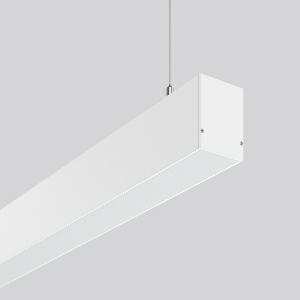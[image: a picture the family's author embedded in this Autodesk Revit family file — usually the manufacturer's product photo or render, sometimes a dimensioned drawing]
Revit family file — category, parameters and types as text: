
# Revit family: less_is_more_50_312313_002_5587
name_source: partatom
category: Lighting Fixtures
units: mm (PartAtom-declared; Revit-internal decimal feet)

## family parameters
Cut with Voids When Loaded = No
Host = Face
Light Source = No
Part Type = Normal
Room Calculation Point = No
Round Connector Dimension = Use Diameter
Shared = No

## types (1)
- LESS IS MORE 50 (1 x LED Modul 830, 3850 lm, 3000)
    Apparent Load = 34 VA
    CIE Flux Codes = 48 79 95 100 100
    Color Rendering = 80
    Color Temperature = 3000
    Default Elevation = 1800 mm
    Description = Series: LESS IS MORE 50
Linear pendant luminaire for aesthetically sophisticated lighting. Housing: extruded aluminium profile, powder-coated. End cap aluminium powder-coated. Canopy made of aluminium, powder-coated. Diffuser made of non-yellowing plastic (PMMA), opal. Direct light emission. Suitable for pendant. 2-point steel cable suspension freely positionable and infinitely height-adjustable. Special lengths available on request. LED unit with integrated converter interchangeable and removable. Suitable for through-wiring. With sensors or as a safety luminaire on request. 
Colour: traffic white, matt (RAL 9016)
Length: 1407 mm
Width: 57 mm
Height: 75 mm
Suspension length: 2000 mm
Lamp: LED
Socket: without socket
Colour temperature: 3000K
Colour rendering index (CRI): 80
System power: 34 W
Rated luminous flux: 3850 lm
Luminous efficiency: 113 lm/W
Control gear: Regulated power supply
Protection class: I
Type of protection: IP 20
    Height = 75 mm
    Lamp = 1 x LED Modul 830
    Lamp Light Flux = 3850 lm
    Lamp count = 1
    Length = 1407 mm
    Lifetime = 50000 h
    Luminous efficacy = 113 lm/W
    Manufacturer = RZB
    ModVariant = No
    Model = 312313.002
    Mounting Place = Ceiling
    Mounting Type = Pendant
    Number of Poles = 1
    OnlyDefault = Yes
    Power Factor = 1
    Product Name = LESS IS MORE 50
    Product group = Pendant LED linear luminaires
    ProductGroupID = 907
    Protection Class = Protection class I
    Protection Degree = IP 20
    RLX_Detail_Level = 1
    RLX_Emergency_Light_Flux = 0 lm
    RLX_Emergency_Type = 0
    RLX_Emergency_Type_DB = No
    RlxData = <blob elided: 20585 chars, md5=db963f38>
    Socket = socket
    Standby Power = 0 W
    System Light Flux = 3850 lm
    System Power = 34 W
    Type Comments = Product without accessories
    Type Image = 312318.002.jpg
    URL = http://relux.com
    VarID = ---
    Voltage = 230 V
    Voltage Range = 220-240 V
    Weight = 0.00 kg
    Width = 57 mm

## geometry (parser evidence)
native form markers: Blend x4, Sweep x11
no freeform markers — native parametric forms only
